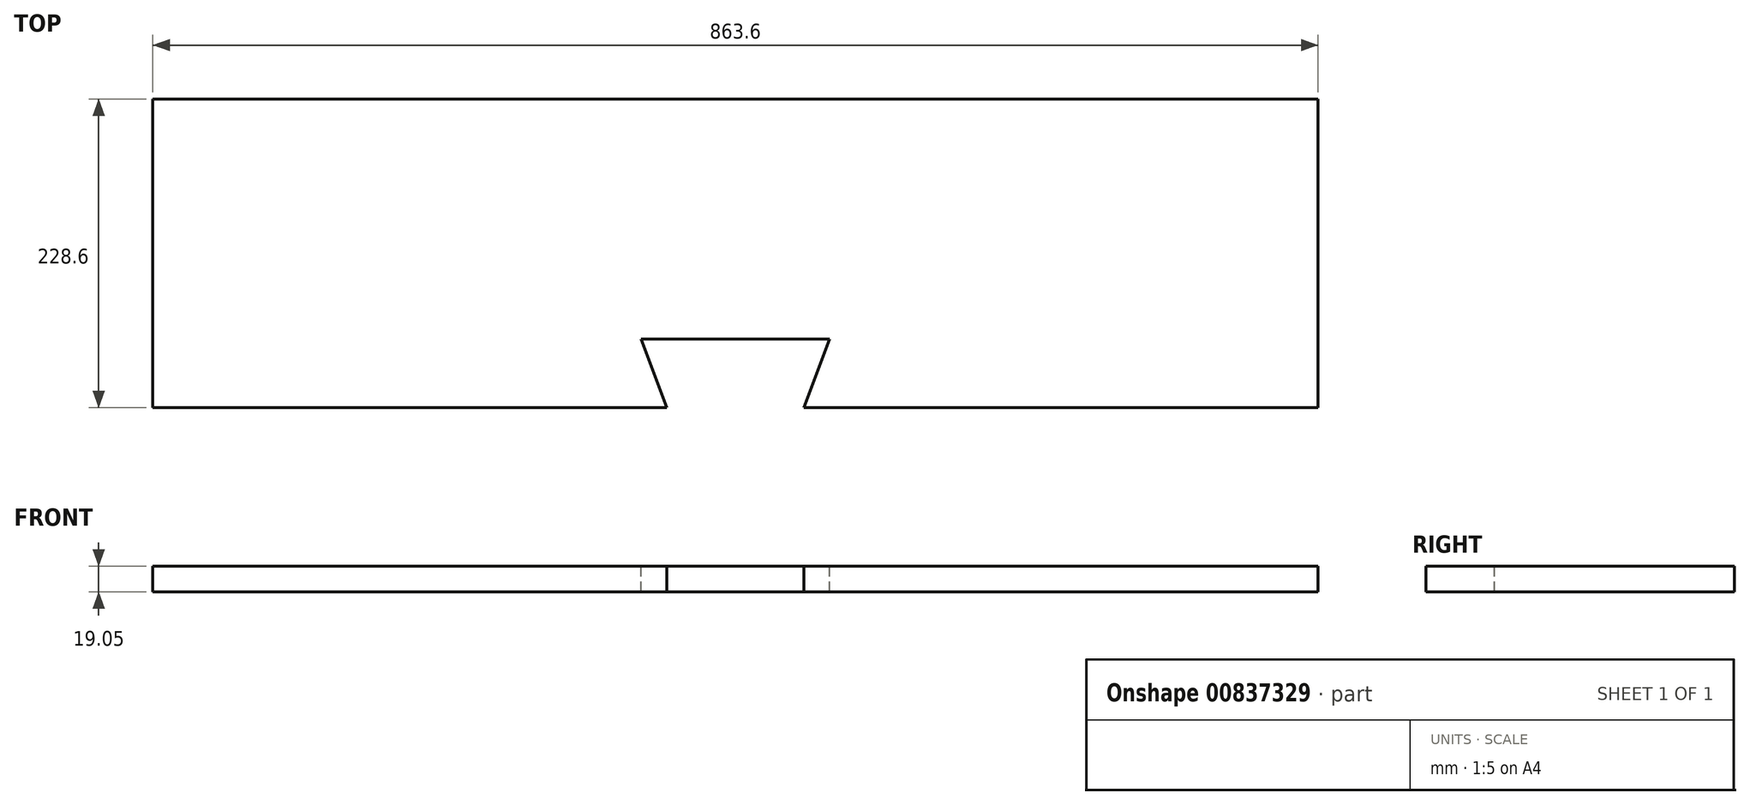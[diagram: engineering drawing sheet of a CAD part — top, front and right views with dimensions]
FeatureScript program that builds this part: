
annotation { "Feature Type Name" : "Feature", "Feature Type Description" : "" }
export const myFeature = defineFeature(function(context is Context, id is Id, definition is map)
    precondition{}
    {
        {
            var Q0;
            Q0=qCreatedBy(makeId("Top.planeOp"),FACE);
            var sketch = newSketch(context, id + "F0", { "sketchPlane" : qUnion([Q0])});
            skLineSegment(sketch, "E0.bottom", {"start": v(-431.8, -228.6) * mm, "end": v(431.8, -228.6) * mm});
            skLineSegment(sketch, "E0.top", {"start": v(-431.8, 0) * mm, "end": v(431.8, 0) * mm});
            skLineSegment(sketch, "E0.left", {"start": v(-431.8, -228.6) * mm, "end": v(-431.8, 0) * mm});
            skLineSegment(sketch, "E0.right", {"start": v(431.8, -228.6) * mm, "end": v(431.8, 0) * mm});
            skSolve(sketch);
        }
        {
            var Q0;
            Q0=makeQuery(id+"F0.imprint","IMPRINT",FACE,{"disambiguationData":[TD([[makeQuery(id+"F0.imprint","IMPRINT",EDGE,{"derivedFrom":sQuery(id+"F0.wireOp",EDGE,"E0.bottom")}),1.0]])]});
            extrude(context, id + "F1", {"entities" : qUnion([Q0]), "depth" : 19.05 * mm, "offsetDistance" : 25.4 * mm});
        }
        {
            var Q0;
            Q0=makeQuery(id+"F1.opExtrude","CAP_FACE",FACE,{"disambiguationData":[OSD([sQuery(id+"F0.wireOp",EDGE,"E0.bottom"),sQuery(id+"F0.wireOp",EDGE,"E0.top"),sQuery(id+"F0.wireOp",EDGE,"E0.left"),sQuery(id+"F0.wireOp",EDGE,"E0.right")])],"isStart":false});
            var sketch = newSketch(context, id + "F2", { "sketchPlane" : qUnion([Q0])});
            skLineSegment(sketch, "E1", {"start": v(-50.8, -228.6) * mm, "end": v(-69.85, -177.8) * mm});
            skLineSegment(sketch, "E2", {"start": v(-69.85, -177.8) * mm, "end": v(69.85, -177.8) * mm});
            skLineSegment(sketch, "E3", {"start": v(69.85, -177.8) * mm, "end": v(50.8, -228.6) * mm});
            skLineSegment(sketch, "E4", {"start": v(50.8, -228.6) * mm, "end": v(-50.8, -228.6) * mm});
            skLineSegment(sketch, "E5", {"start": v(0, 0) * mm, "end": v(0, -228.6) * mm, "construction": true});
            skSolve(sketch);
        }
        {
            var Q0;
            Q0=makeQuery(id+"F2.imprint","IMPRINT",FACE,{"disambiguationData":[TD([[makeQuery(id+"F2.imprint","IMPRINT",EDGE,{"derivedFrom":sQuery(id+"F2.wireOp",EDGE,"E1")}),-1.0]])]});
            extrude(context, id + "F3", {"entities" : qUnion([Q0]), "operationType" : NewBodyOperationType.REMOVE, "endBound" : BoundingType.THROUGH_ALL, "oppositeDirection" : true, "depth" : 25.4 * mm, "offsetDistance" : 25.4 * mm});
        }
    });
